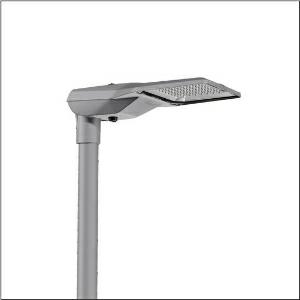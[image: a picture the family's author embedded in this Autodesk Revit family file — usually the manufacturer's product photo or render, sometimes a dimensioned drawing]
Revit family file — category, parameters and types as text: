
# Revit family: streetlight_sl_21_midi___st1_0ab_5xe3m33t08nb_9bc9
name_source: partatom
category: Lighting Fixtures
units: mm (PartAtom-declared; Revit-internal decimal feet)

## family parameters
Cut with Voids When Loaded = No
Host = Face
Light Source = No
Part Type = Normal
Room Calculation Point = No
Round Connector Dimension = Use Diameter
Shared = No

## types (1)
- --- (1 x LED, 19980 lm, 151.2 W, 3000K)
    Apparent Load = 151 VA
    CIE Flux Codes = 40 74 97 100 100
    Color Rendering = 70
    Color Temperature = 3000K
    Default Elevation = 1800 mm
    Description = Streetlight SL 21 midi, mast luminaire, primary light control with lens, of PMMA, primary optical cover: cover, of toughened safety glass, transparent, light distribution: ST1.0aB, light emission: direct distribution, primary light characteristic: asymmetric, installation type: side-entry, post-top, LED, High Power LED, rated luminous flux: 19.980lm, luminous efficacy: 132lm/W, light colour: 730, colour temperature: 3000K, control gear: D4i, control: flexible luminous flux parameterisation, time-dependent luminous flux control, constant luminous flux control, overheat protection, pre-setting: logarithmic dimming characteristic, mains connection: 230..240V, AC, 50/60Hz, start of lifetime: 151W, end of service life: 157W, reduction: 70W, luminaire housing, of diecast aluminium, powder-coated, SITECO metallic grey (DB 702S), corrosivity category C5 high according to DIN EN ISO 12944, please order mast flange separately, inclination adjustable: 0°, 5°, 10°, 15°, sealing non-destructively replaceable, multi-level sealing system, length: 644mm, width: 335mm, height: 110mm, mast flange for spigot size: 42mm (side-entry): 5XC10008XM4, 60/48mm (side-entry/post-top): 5XC10108XM2, 76/60mm (side-entry/post-top): 5XC10108XM1, mounting height: 4..8m, Smart Interface below and above, protection rating (complete): IP66, insulation class (complete): insulation class II (safety insulation), certification: CE, ENEC, ENEC+, VDE, impact resistance: IK10, permissible operating ambient temperature for outdoor applications: -40..+50°C, standard-compliant lighting for roads and squares, packaging unit: 1 piece

Light Distribution: ST1.0aB
    Height = 111 mm
    Lamp = 1 x LED
    Lamp Light Flux = 19980 lm
    Lamp Power = 151.2 W
    Lamp count = 1
    Length = 644 mm
    Luminous efficacy = 132 lm/W
    Manufacturer = Siteco
    ModVariant = No
    Model = 5XE3M33T08NB
    Number of Poles = 1
    OnlyDefault = Yes
    Power Factor = 1
    Product Name = Streetlight SL 21 midi | ST1.0aB
    Product group = mast luminaire | pylon top
    ProductGroupID = 6100
    Protection Class = Protection class II
    Protection Degree = IP 66
    RLX_Detail_Level = 1
    RLX_Emergency_Light_Flux = 0 lm
    RLX_Emergency_Type = 0
    RLX_Emergency_Type_DB = No
    RlxData = <blob elided: 27065 chars, md5=3855f30e>
    Socket = socket
    Standby Power = 0 W
    System Light Flux = 19980 lm
    System Power = 151 W
    Type Comments = factory setting: luminous flux: 100 % | dim-lin: 254 | 802 mA
    Type Image = l_1004304.jpg
    URL = http://relux.com
    VarID = @adj_167585
    Voltage = 0 V
    Weight = 0.00 kg
    Width = 336 mm

## geometry (parser evidence)
native form markers: Blend x4, Sweep x11
no freeform markers — native parametric forms only
